# Revit family: DC_Rheem_PLM_HeatPump_953022_Horizontal_12
name_source: partatom
category: Plumbing Fixtures
revit_build: Autodesk Revit Architecture 2012 (Build: 20110916_2132(x64)
units: mm (PartAtom-declared; Revit-internal decimal feet)

## types (1)
- Commercial Heat Pump - Non Ducted
    CDPipeRadius_ANZRS = 10 mm  [stored 0.0328084 ft]
    CondensateDrainPipeDiameter_ANZRS = 20 mm  [stored 0.0656168 ft]
    Description = Commercial Heat Pump - Non Ducted
    InPipeRadius_ANZRS = 16 mm  [stored 0.0524934 ft]
    InletPipeDiameter_ANZRS = 32 mm
    Manufacturer = Rheem
    Materials_ANZRS = Rheem - Joey Grey Steel
    Model = 953022
    OutPipeRadius_ANZRS = 16 mm  [stored 0.0524934 ft]
    OutletPipeDiameter_ANZRS = 32 mm
    Type Comments = Output 16 KW @ 20oC/60% RH Recovery 300 L/h  @ 45°C  rise
    URL = http://www.rheem.com.au
    UnitWidth_ANZRS = 565 mm
    Unitheight_ANZRS = 935 mm  [stored 3.06759 ft]

note: [stored X ft] marks values corroborated as IEEE doubles in the binary element streams (Revit-internal decimal feet)

## geometry (parser evidence)
native form markers: Blend x8, Sweep x4
no freeform markers — native parametric forms only
